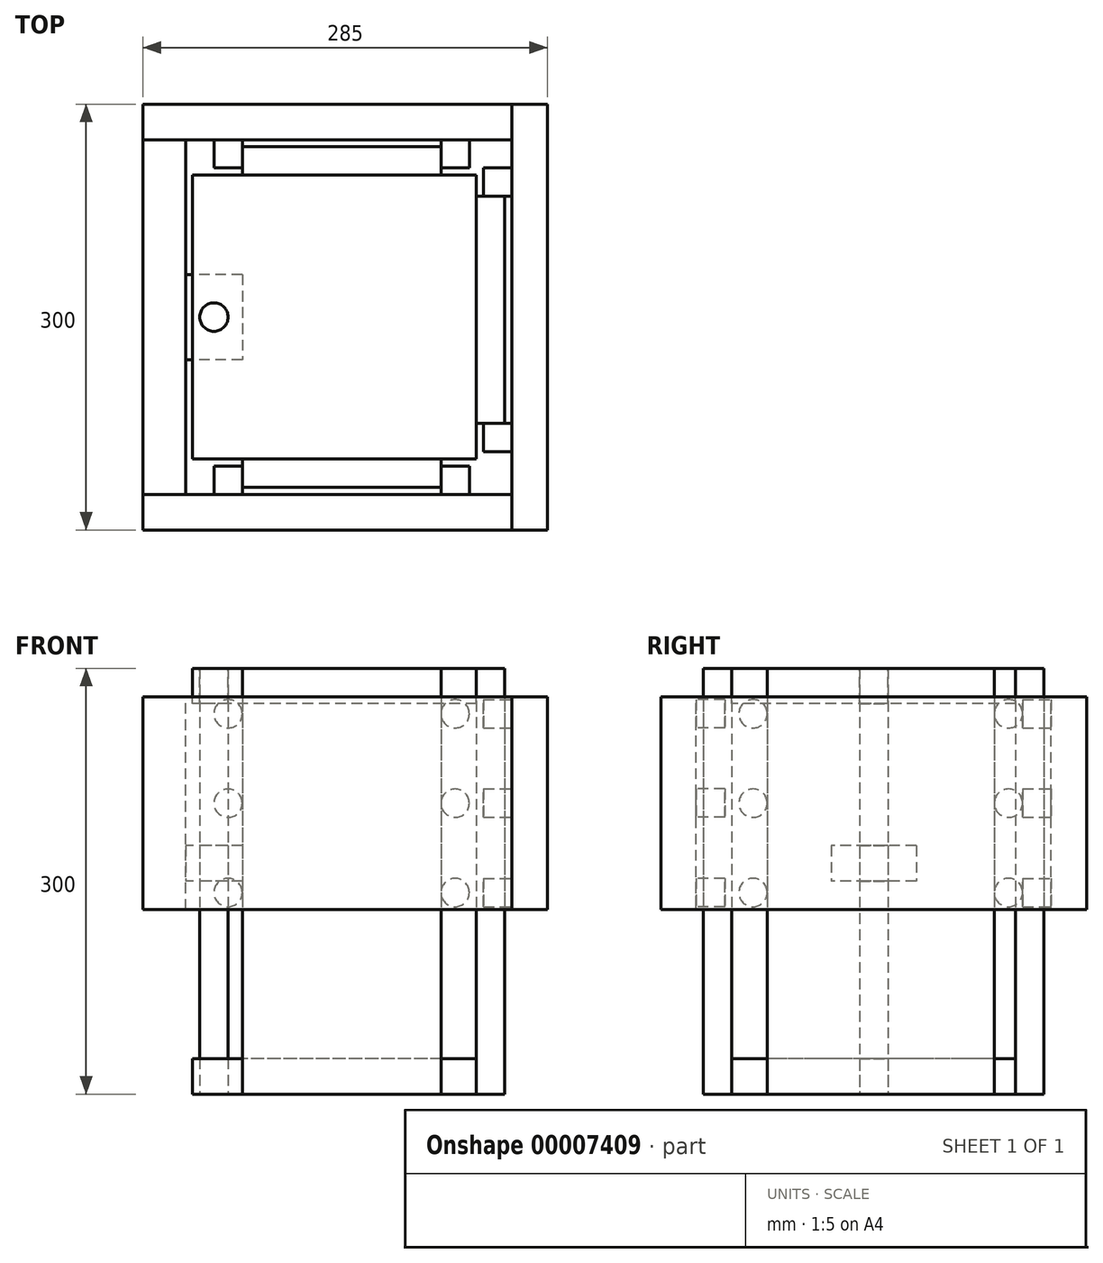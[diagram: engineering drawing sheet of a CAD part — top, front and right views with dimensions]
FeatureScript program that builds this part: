
annotation { "Feature Type Name" : "Feature", "Feature Type Description" : "" }
export const myFeature = defineFeature(function(context is Context, id is Id, definition is map)
    precondition{}
    {
        {
            var Q0;
            Q0=qCreatedBy(makeId("Top.planeOp"),FACE);
            var sketch = newSketch(context, id + "F0", { "sketchPlane" : qUnion([Q0])});
            skCircle(sketch, "E0", {"center": v(0, 0) * mm, "radius": 10 * mm});
            skSolve(sketch);
        }
        {
            var Q0;
            Q0=makeQuery(id+"F0.imprint","IMPRINT",FACE,{"disambiguationData":[TD([[makeQuery(id+"F0.imprint","IMPRINT",EDGE,{"derivedFrom":sQuery(id+"F0.wireOp",EDGE,"E0")}),1.0]])]});
            extrude(context, id + "F1", {"entities" : qUnion([Q0]), "depth" : 300 * mm});
        }
        {
            var Q0;
            Q0=makeQuery(id+"F1.opExtrude","CAP_FACE",FACE,{"disambiguationData":[OSD([sQuery(id+"F0.wireOp",EDGE,"E0")])],"isStart":false});
            var Q1;
            Q1=makeQuery(id+"F1.opExtrude","CAP_FACE",FACE,{"disambiguationData":[OSD([sQuery(id+"F0.wireOp",EDGE,"E0")])],"isStart":true});
            cPlane(context, id + "F2", {"entities" : qUnion([Q0, Q1]), "cplaneType" : CPlaneType.MID_PLANE, "offset" : 150 * mm, "width" : 150 * mm, "height" : 150 * mm});
        }
        {
            var Q0;
            Q0=qCreatedBy(id+"F2.planeOp",FACE);
            var sketch = newSketch(context, id + "F3", { "sketchPlane" : qUnion([Q0])});
            skCircle(sketch, "E1.0", {"center": v(0, 0) * mm, "radius": 10 * mm, "construction": true});
            skLineSegment(sketch, "E2.rect.bottom", {"start": v(20, 30) * mm, "end": v(-20, 30) * mm});
            skLineSegment(sketch, "E2.rect.top", {"start": v(20, -30) * mm, "end": v(-20, -30) * mm});
            skLineSegment(sketch, "E2.rect.left", {"start": v(20, 30) * mm, "end": v(20, -30) * mm});
            skLineSegment(sketch, "E2.rect.right", {"start": v(-20, 30) * mm, "end": v(-20, -30) * mm});
            skSolve(sketch);
        }
        {
            var Q0;
            Q0 = qSketchRegion(id + "F3", true);
            extrude(context, id + "F4", {"entities" : qUnion([Q0]), "depth" : 25 * mm});
        }
        {
            var Q0;
            Q0=makeQuery(id+"F1.opExtrude","SWEPT_BODY",BODY,{"disambiguationData":[OSD([sQuery(id+"F0.wireOp",EDGE,"E0")])]});
            var Q1;
            Q1=makeQuery(id+"F4.opExtrude","SWEPT_BODY",BODY,{"disambiguationData":[OSD([sQuery(id+"F3.wireOp",EDGE,"E2.rect.bottom"),sQuery(id+"F3.wireOp",EDGE,"E2.rect.top"),sQuery(id+"F3.wireOp",EDGE,"E2.rect.left"),sQuery(id+"F3.wireOp",EDGE,"E2.rect.right")])]});
            booleanBodies(context, id + "F5", {"operationType" : BooleanOperationType.SUBTRACTION, "tools" : qUnion([Q0]), "targets" : qUnion([Q1]), "keepTools" : true});
        }
        {
            var Q0;
            Q0=makeQuery(id+"F1.opExtrude","CAP_FACE",FACE,{"disambiguationData":[OSD([sQuery(id+"F0.wireOp",EDGE,"E0")])],"isStart":false});
            var sketch = newSketch(context, id + "F6", { "sketchPlane" : qUnion([Q0])});
            skLineSegment(sketch, "E3.bottom", {"start": v(185, 100) * mm, "end": v(-15, 100) * mm});
            skLineSegment(sketch, "E3.top", {"start": v(185, -100) * mm, "end": v(-15, -100) * mm});
            skLineSegment(sketch, "E3.left", {"start": v(185, 100) * mm, "end": v(185, -100) * mm});
            skLineSegment(sketch, "E3.right", {"start": v(-15, 100) * mm, "end": v(-15, -100) * mm});
            skLineSegment(sketch, "E4", {"start": v(-15, 0) * mm, "end": v(0, 0) * mm});
            skSolve(sketch);
        }
        {
            var Q0;
            {var subQ3=sQuery(id+"F6.wireOp",EDGE,"E3.bottom");Q0=makeQuery(id+"F6.imprint","IMPRINT",FACE,{"disambiguationData":[TD([[makeQuery(id+"F6.imprint","IMPRINT",EDGE,{"derivedFrom":subQ3}),1.0]])]});}
            extrude(context, id + "F7", {"entities" : qUnion([Q0]), "oppositeDirection" : true, "depth" : 25 * mm});
        }
        {
            var Q0;
            Q0=makeQuery(id+"F1.opExtrude","CAP_FACE",FACE,{"disambiguationData":[OSD([sQuery(id+"F0.wireOp",EDGE,"E0")])],"isStart":true});
            var sketch = newSketch(context, id + "F8", { "sketchPlane" : qUnion([Q0])});
            skLineSegment(sketch, "E5.0", {"start": v(185, 100) * mm, "end": v(-15, 100) * mm});
            skLineSegment(sketch, "E5.1", {"start": v(-15, -100) * mm, "end": v(-15, 100) * mm});
            skLineSegment(sketch, "E5.2", {"start": v(185, -100) * mm, "end": v(185, 100) * mm});
            skLineSegment(sketch, "E5.3", {"start": v(185, -100) * mm, "end": v(-15, -100) * mm});
            skSolve(sketch);
        }
        {
            var Q0;
            Q0=makeQuery(id+"F8.imprint","IMPRINT",FACE,{"disambiguationData":[TD([[makeQuery(id+"F8.imprint","IMPRINT",EDGE,{"derivedFrom":sQuery(id+"F8.wireOp",EDGE,"E5.0")}),1.0]])]});
            extrude(context, id + "F9", {"entities" : qUnion([Q0]), "oppositeDirection" : true, "depth" : 25 * mm});
        }
        {
            var Q0;
            Q0=makeQuery(id+"F4.opExtrude","SWEPT_FACE",FACE,{"disambiguationData":[OSD([sQuery(id+"F3.wireOp",EDGE,"E2.rect.right")])]});
            var sketch = newSketch(context, id + "F10", { "sketchPlane" : qUnion([Q0])});
            skLineSegment(sketch, "E6.bottom", {"start": v(-125, 130) * mm, "end": v(125, 130) * mm});
            skLineSegment(sketch, "E6.top", {"start": v(-125, 280) * mm, "end": v(125, 280) * mm});
            skLineSegment(sketch, "E6.left", {"start": v(-125, 130) * mm, "end": v(-125, 280) * mm});
            skLineSegment(sketch, "E6.right", {"start": v(125, 130) * mm, "end": v(125, 280) * mm});
            skLineSegment(sketch, "E7", {"start": v(0, 150) * mm, "end": v(0, 130) * mm, "construction": true});
            skSolve(sketch);
        }
        {
            var Q0;
            Q0=makeQuery(id+"F10.imprint","IMPRINT",FACE,{"disambiguationData":[TD([[makeQuery(id+"F10.imprint","IMPRINT",EDGE,{"derivedFrom":sQuery(id+"F10.wireOp",EDGE,"E6.bottom")}),1.0]])]});
            var Q1;
            {var subQ0=sQuery(id+"F3.wireOp",EDGE,"E2.rect.right");Q1=makeQuery(id+"F10.imprint","IMPRINT",FACE,{"disambiguationData":[TD([[makeQuery(id+"F10.imprint","IMPRINT",EDGE,{"derivedFrom":makeQuery(id+"F4.opExtrude","CAP_EDGE",EDGE,{"disambiguationData":[OSD([subQ0])],"isStart":true})}),1.0]])]});}
            extrude(context, id + "F11", {"entities" : qUnion([Q0, Q1]), "depth" : 30 * mm});
        }
        {
            var Q0;
            Q0=makeQuery(id+"F11.opExtrude","SWEPT_FACE",FACE,{"disambiguationData":[OSD([sQuery(id+"F10.wireOp",EDGE,"E6.right")])]});
            var sketch = newSketch(context, id + "F12", { "sketchPlane" : qUnion([Q0])});
            skLineSegment(sketch, "E8.bottom", {"start": v(-50, 130) * mm, "end": v(210, 130) * mm});
            skLineSegment(sketch, "E8.top", {"start": v(-50, 280) * mm, "end": v(210, 280) * mm});
            skLineSegment(sketch, "E8.left", {"start": v(-50, 130) * mm, "end": v(-50, 280) * mm});
            skLineSegment(sketch, "E8.right", {"start": v(210, 130) * mm, "end": v(210, 280) * mm});
            skSolve(sketch);
        }
        {
            var Q0;
            Q0 = qSketchRegion(id + "F12", true);
            extrude(context, id + "F13", {"entities" : qUnion([Q0]), "depth" : 25 * mm});
        }
        {
            var Q0;
            Q0=makeQuery(id+"F13.opExtrude","CAP_FACE",FACE,{"disambiguationData":[OSD([sQuery(id+"F12.wireOp",EDGE,"E8.bottom"),sQuery(id+"F12.wireOp",EDGE,"E8.top"),sQuery(id+"F12.wireOp",EDGE,"E8.left"),sQuery(id+"F12.wireOp",EDGE,"E8.right")])],"isStart":true});
            var sketch = newSketch(context, id + "F14", { "sketchPlane" : qUnion([Q0])});
            skCircle(sketch, "E9", {"center": v(-10, 268) * mm, "radius": 10 * mm});
            skLineSegment(sketch, "E10", {"start": v(0, 268) * mm, "end": v(20, 268) * mm});
            skLineSegment(sketch, "E11", {"start": v(-10, 278) * mm, "end": v(-10, 280) * mm});
            skCircle(sketch, "E12.0.1.0", {"center": v(-10, 205) * mm, "radius": 10 * mm});
            skCircle(sketch, "E12.0.2.0", {"center": v(-10, 142) * mm, "radius": 10 * mm});
            skCircle(sketch, "E12.1.0.0", {"center": v(-170, 268) * mm, "radius": 10 * mm});
            skCircle(sketch, "E12.1.1.0", {"center": v(-170, 205) * mm, "radius": 10 * mm});
            skCircle(sketch, "E12.1.2.0", {"center": v(-170, 142) * mm, "radius": 10 * mm});
            skLineSegment(sketch, "E12.direction1", {"start": v(-10, 268) * mm, "end": v(-170, 268) * mm, "construction": true});
            skLineSegment(sketch, "E12.direction2", {"start": v(-10, 268) * mm, "end": v(-10, 205) * mm, "construction": true});
            skLineSegment(sketch, "E13", {"start": v(-180, 268) * mm, "end": v(-210, 268) * mm, "construction": true});
            skLineSegment(sketch, "E14", {"start": v(-10, 132) * mm, "end": v(-10, 130) * mm, "construction": true});
            skLineSegment(sketch, "E15", {"start": v(-170, 268) * mm, "end": v(-170, 205) * mm, "construction": true});
            skSolve(sketch);
        }
        {
            var Q0;
            {var subQ0=sQuery(id+"F14.wireOp",EDGE,"E9");var subQ2=makeQuery(id+"F14.imprint","IMPRINT",VERTEX,{"disambiguationData":[OD(0.0)],"derivedFrom":subQ0});Q0=makeQuery(id+"F14.imprint","IMPRINT",FACE,{"disambiguationData":[TD([[makeQuery(id+"F14.imprint","IMPRINT",EDGE,{"disambiguationData":[TD([[subQ2,-1.0]])],"derivedFrom":subQ0}),1.0]])]});}
            var Q1;
            Q1=makeQuery(id+"F14.imprint","IMPRINT",FACE,{"disambiguationData":[TD([[makeQuery(id+"F14.imprint","IMPRINT",EDGE,{"derivedFrom":sQuery(id+"F14.wireOp",EDGE,"E12.1.0.0")}),1.0]])]});
            var Q2;
            Q2=makeQuery(id+"F14.imprint","IMPRINT",FACE,{"disambiguationData":[TD([[makeQuery(id+"F14.imprint","IMPRINT",EDGE,{"derivedFrom":sQuery(id+"F14.wireOp",EDGE,"E12.1.1.0")}),1.0]])]});
            var Q3;
            Q3=makeQuery(id+"F14.imprint","IMPRINT",FACE,{"disambiguationData":[TD([[makeQuery(id+"F14.imprint","IMPRINT",EDGE,{"derivedFrom":sQuery(id+"F14.wireOp",EDGE,"E12.1.2.0")}),1.0]])]});
            var Q4;
            Q4=makeQuery(id+"F14.imprint","IMPRINT",FACE,{"disambiguationData":[TD([[makeQuery(id+"F14.imprint","IMPRINT",EDGE,{"derivedFrom":sQuery(id+"F14.wireOp",EDGE,"E12.0.2.0")}),1.0]])]});
            var Q5;
            Q5=makeQuery(id+"F14.imprint","IMPRINT",FACE,{"disambiguationData":[TD([[makeQuery(id+"F14.imprint","IMPRINT",EDGE,{"derivedFrom":sQuery(id+"F14.wireOp",EDGE,"E12.0.1.0")}),1.0]])]});
            extrude(context, id + "F15", {"entities" : qUnion([Q0, Q1, Q2, Q3, Q4, Q5]), "depth" : 20 * mm});
        }
        {
            var Q0;
            Q0=makeQuery(id+"F7.opExtrude","SWEPT_FACE",FACE,{"disambiguationData":[OSD([sQuery(id+"F6.wireOp",EDGE,"E3.top")])]});
            var sketch = newSketch(context, id + "F16", { "sketchPlane" : qUnion([Q0])});
            skLineSegment(sketch, "E16.bottom", {"start": v(20, 300) * mm, "end": v(160, 300) * mm});
            skLineSegment(sketch, "E16.top", {"start": v(20, 0) * mm, "end": v(160, 0) * mm});
            skLineSegment(sketch, "E16.left", {"start": v(20, 300) * mm, "end": v(20, 0) * mm});
            skLineSegment(sketch, "E16.right", {"start": v(160, 300) * mm, "end": v(160, 0) * mm});
            skSolve(sketch);
        }
        {
            var Q0;
            Q0 = qSketchRegion(id + "F16", true);
            extrude(context, id + "F17", {"entities" : qUnion([Q0]), "depth" : 20 * mm});
        }
        {
            var Q0;
            Q0=makeQuery(id+"F13.opExtrude","SWEPT_FACE",FACE,{"disambiguationData":[OSD([sQuery(id+"F12.wireOp",EDGE,"E8.right")])]});
            var sketch = newSketch(context, id + "F18", { "sketchPlane" : qUnion([Q0])});
            skLineSegment(sketch, "E17.bottom", {"start": v(-150, 130) * mm, "end": v(150, 130) * mm});
            skLineSegment(sketch, "E17.top", {"start": v(-150, 280) * mm, "end": v(150, 280) * mm});
            skLineSegment(sketch, "E17.left", {"start": v(-150, 130) * mm, "end": v(-150, 280) * mm});
            skLineSegment(sketch, "E17.right", {"start": v(150, 130) * mm, "end": v(150, 280) * mm});
            skSolve(sketch);
        }
        {
            var Q0;
            Q0 = qSketchRegion(id + "F18", true);
            extrude(context, id + "F19", {"entities" : qUnion([Q0]), "depth" : 25 * mm});
        }
        {
            var Q0;
            Q0=makeQuery(id+"F19.opExtrude","CAP_FACE",FACE,{"disambiguationData":[OSD([sQuery(id+"F18.wireOp",EDGE,"E17.bottom"),sQuery(id+"F18.wireOp",EDGE,"E17.top"),sQuery(id+"F18.wireOp",EDGE,"E17.left"),sQuery(id+"F18.wireOp",EDGE,"E17.right")])],"isStart":true});
            var sketch = newSketch(context, id + "F20", { "sketchPlane" : qUnion([Q0])});
            skCircle(sketch, "E18", {"center": v(85, 268) * mm, "radius": 10 * mm});
            skLineSegment(sketch, "E19", {"start": v(95, 268) * mm, "end": v(125, 268) * mm, "construction": true});
            skLineSegment(sketch, "E20", {"start": v(85, 278) * mm, "end": v(85, 280) * mm, "construction": true});
            skCircle(sketch, "E21.0.1.0", {"center": v(85, 205) * mm, "radius": 10 * mm});
            skCircle(sketch, "E21.0.2.0", {"center": v(85, 142) * mm, "radius": 10 * mm});
            skCircle(sketch, "E21.1.0.0", {"center": v(-95, 268) * mm, "radius": 10 * mm});
            skCircle(sketch, "E21.1.1.0", {"center": v(-95, 205) * mm, "radius": 10 * mm});
            skCircle(sketch, "E21.1.2.0", {"center": v(-95, 142) * mm, "radius": 10 * mm});
            skLineSegment(sketch, "E21.direction1", {"start": v(85, 268) * mm, "end": v(-95, 268) * mm, "construction": true});
            skLineSegment(sketch, "E21.direction2", {"start": v(85, 268) * mm, "end": v(85, 205) * mm, "construction": true});
            skLineSegment(sketch, "E22", {"start": v(85, 132) * mm, "end": v(85, 130) * mm, "construction": true});
            skSolve(sketch);
        }
        {
            var Q0;
            Q0=makeQuery(id+"F20.imprint","IMPRINT",FACE,{"disambiguationData":[TD([[makeQuery(id+"F20.imprint","IMPRINT",EDGE,{"derivedFrom":sQuery(id+"F20.wireOp",EDGE,"E18")}),1.0]])]});
            var Q1;
            Q1=makeQuery(id+"F20.imprint","IMPRINT",FACE,{"disambiguationData":[TD([[makeQuery(id+"F20.imprint","IMPRINT",EDGE,{"derivedFrom":sQuery(id+"F20.wireOp",EDGE,"E21.1.0.0")}),1.0]])]});
            var Q2;
            Q2=makeQuery(id+"F20.imprint","IMPRINT",FACE,{"disambiguationData":[TD([[makeQuery(id+"F20.imprint","IMPRINT",EDGE,{"derivedFrom":sQuery(id+"F20.wireOp",EDGE,"E21.1.1.0")}),1.0]])]});
            var Q3;
            Q3=makeQuery(id+"F20.imprint","IMPRINT",FACE,{"disambiguationData":[TD([[makeQuery(id+"F20.imprint","IMPRINT",EDGE,{"derivedFrom":sQuery(id+"F20.wireOp",EDGE,"E21.0.1.0")}),1.0]])]});
            var Q4;
            Q4=makeQuery(id+"F20.imprint","IMPRINT",FACE,{"disambiguationData":[TD([[makeQuery(id+"F20.imprint","IMPRINT",EDGE,{"derivedFrom":sQuery(id+"F20.wireOp",EDGE,"E21.0.2.0")}),1.0]])]});
            var Q5;
            Q5=makeQuery(id+"F20.imprint","IMPRINT",FACE,{"disambiguationData":[TD([[makeQuery(id+"F20.imprint","IMPRINT",EDGE,{"derivedFrom":sQuery(id+"F20.wireOp",EDGE,"E21.1.2.0")}),1.0]])]});
            extrude(context, id + "F21", {"entities" : qUnion([Q0, Q1, Q2, Q3, Q4, Q5]), "depth" : 20 * mm});
        }
        {
            var Q0;
            Q0=makeQuery(id+"F7.opExtrude","SWEPT_FACE",FACE,{"disambiguationData":[OSD([sQuery(id+"F6.wireOp",EDGE,"E3.left")])]});
            var sketch = newSketch(context, id + "F22", { "sketchPlane" : qUnion([Q0])});
            skLineSegment(sketch, "E23.bottom", {"start": v(-75, 300) * mm, "end": v(85, 300) * mm});
            skLineSegment(sketch, "E23.top", {"start": v(-75, 0) * mm, "end": v(85, 0) * mm});
            skLineSegment(sketch, "E23.left", {"start": v(-75, 300) * mm, "end": v(-75, 0) * mm});
            skLineSegment(sketch, "E23.right", {"start": v(85, 300) * mm, "end": v(85, 0) * mm});
            skSolve(sketch);
        }
        {
            var Q0;
            Q0 = qSketchRegion(id + "F22", true);
            extrude(context, id + "F23", {"entities" : qUnion([Q0]), "depth" : 20 * mm});
        }
        {
            var Q0;
            Q0=makeQuery(id+"F11.opExtrude","SWEPT_FACE",FACE,{"disambiguationData":[OSD([sQuery(id+"F10.wireOp",EDGE,"E6.left")])]});
            var sketch = newSketch(context, id + "F24", { "sketchPlane" : qUnion([Q0])});
            skLineSegment(sketch, "E24.bottom", {"start": v(50, 280) * mm, "end": v(-210, 280) * mm});
            skLineSegment(sketch, "E24.top", {"start": v(50, 130) * mm, "end": v(-210, 130) * mm});
            skLineSegment(sketch, "E24.left", {"start": v(50, 280) * mm, "end": v(50, 130) * mm});
            skLineSegment(sketch, "E24.right", {"start": v(-210, 280) * mm, "end": v(-210, 130) * mm});
            skSolve(sketch);
        }
        {
            var Q0;
            Q0 = qSketchRegion(id + "F24", true);
            extrude(context, id + "F25", {"entities" : qUnion([Q0]), "depth" : 25 * mm});
        }
        {
            var Q0;
            Q0=makeQuery(id+"F7.opExtrude","SWEPT_FACE",FACE,{"disambiguationData":[OSD([sQuery(id+"F6.wireOp",EDGE,"E3.bottom")])]});
            var Q1;
            Q1=makeQuery(id+"F7.opExtrude","SWEPT_FACE",FACE,{"disambiguationData":[OSD([sQuery(id+"F6.wireOp",EDGE,"E3.top")])]});
            cPlane(context, id + "F26", {"entities" : qUnion([Q0, Q1]), "cplaneType" : CPlaneType.MID_PLANE, "offset" : 150 * mm, "width" : 150 * mm, "height" : 150 * mm});
        }
        {
            var Q0;
            Q0=makeQuery(id+"F17.opExtrude","SWEPT_BODY",BODY,{"disambiguationData":[OSD([sQuery(id+"F16.wireOp",EDGE,"E16.bottom"),sQuery(id+"F16.wireOp",EDGE,"E16.top"),sQuery(id+"F16.wireOp",EDGE,"E16.left"),sQuery(id+"F16.wireOp",EDGE,"E16.right")])]});
            var Q1;
            Q1=makeQuery(id+"F15.opExtrude","SWEPT_BODY",BODY,{"disambiguationData":[OSD([sQuery(id+"F14.wireOp",EDGE,"E12.1.0.0")])]});
            var Q2;
            Q2=makeQuery(id+"F15.opExtrude","SWEPT_BODY",BODY,{"disambiguationData":[OSD([sQuery(id+"F14.wireOp",EDGE,"E12.1.1.0")])]});
            var Q3;
            Q3=makeQuery(id+"F15.opExtrude","SWEPT_BODY",BODY,{"disambiguationData":[OSD([sQuery(id+"F14.wireOp",EDGE,"E12.1.2.0")])]});
            var Q4;
            Q4=makeQuery(id+"F15.opExtrude","SWEPT_BODY",BODY,{"disambiguationData":[OSD([sQuery(id+"F14.wireOp",EDGE,"E12.0.2.0")])]});
            var Q5;
            Q5=makeQuery(id+"F15.opExtrude","SWEPT_BODY",BODY,{"disambiguationData":[OSD([sQuery(id+"F14.wireOp",EDGE,"E12.0.1.0")])]});
            var Q6;
            Q6=makeQuery(id+"F15.opExtrude","SWEPT_BODY",BODY,{"disambiguationData":[OSD([sQuery(id+"F14.wireOp",EDGE,"E9")])]});
            var Q7;
            Q7=qCreatedBy(id+"F26.planeOp",FACE);
            mirror(context, id + "F27", {"entities" : qUnion([Q0, Q1, Q2, Q3, Q4, Q5, Q6]), "mirrorPlane" : qUnion([Q7])});
        }
    });
